# Revit family: Screen_Door_ProfessionalSeries_PhantomScreen
name_source: partatom
category: Doors
revit_build: Autodesk Revit 2014 (Build: 20130308_1515(x64)
units: mm (PartAtom-declared; Revit-internal decimal feet)

## types (1)
- Type as Specified
    Aluminum Housing = Dark Cherry
    Aluminum Track = Aluminum - Flat
    Assembly Code = B2020400
    Construction Details = http://www.arcat.com
    Description = Phantom Screens Professional Series Screen
    Function = Interior
    Handle Depth = 0' - 0 27/32"
    Handle Height = 0' - 6 1/32"
    Handle Width = 0' - 1 9/32"
    Height = 8' - 0"
    Housing Depth = 0' - 2 25/32"
    Housing Width = 0' - 1 7/8"
    Installation-Fabrication = http://www.phantomscreens.com
    Keynote = 08 11 00
    Manufacturer = Phantom Screens
    Manufacturer Fax = 604-855-7834
    Manufacturer Website = http://www.phantomscreens.com
    Model = Professional Series
    Product Data = http://www.arcat.com
    Product Properties = http://www.phantomscreens.com
    Revision = R1_08-2016
    Sales Information = http://www.phantomscreens.com
    Screen = Phifer TuffScreen No-See-Um – Charcoal
    Screen Thickness = 0' - 0 1/32"
    Slide Bar = Dark Cherry
    Slide Bar Depth = 0' - 0 7/8"
    Slide Bar Width = 0' - 1 23/32"
    Specification = http://www.phantomscreens.com
    Track Depth = 0' - 0 1/2"
    Track Height = 0' - 0 15/16"
    URL = http://www.phantomscreens.com
    Wall Closure = By host
    Width = 5' - 0"

## geometry (parser evidence)
native form markers: Sweep x12
no freeform markers — native parametric forms only
